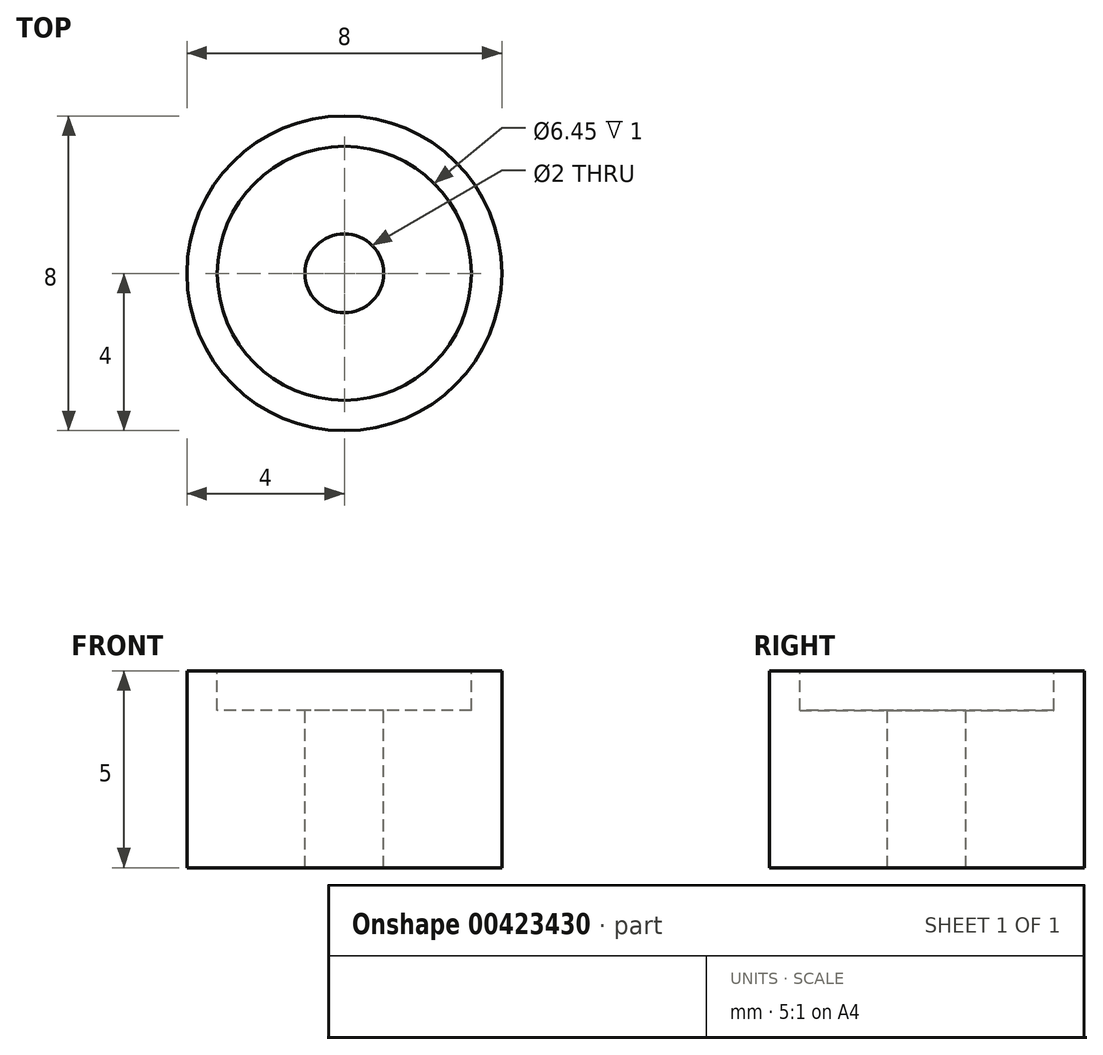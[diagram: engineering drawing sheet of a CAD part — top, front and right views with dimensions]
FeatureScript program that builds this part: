
annotation { "Feature Type Name" : "Feature", "Feature Type Description" : "" }
export const myFeature = defineFeature(function(context is Context, id is Id, definition is map)
    precondition{}
    {
        {
            var Q0;
            Q0=qCreatedBy(makeId("Top.planeOp"),FACE);
            var sketch = newSketch(context, id + "F0", { "sketchPlane" : qUnion([Q0])});
            skCircle(sketch, "E0", {"center": v(0, 0) * mm, "radius": 4 * mm});
            skSolve(sketch);
        }
        {
            var Q0;
            Q0 = qSketchRegion(id + "F0", true);
            extrude(context, id + "F1", {"entities" : qUnion([Q0]), "depth" : 5 * mm});
        }
        {
            var Q0;
            Q0=makeQuery(id+"F1.opExtrude","CAP_FACE",FACE,{"disambiguationData":[OSD([sQuery(id+"F0.wireOp",EDGE,"E0")])],"isStart":false});
            var sketch = newSketch(context, id + "F2", { "sketchPlane" : qUnion([Q0])});
            skCircle(sketch, "E1", {"center": v(0, 0) * mm, "radius": 3.23 * mm});
            skSolve(sketch);
        }
        {
            var Q0;
            Q0 = qSketchRegion(id + "F2", true);
            extrude(context, id + "F3", {"entities" : qUnion([Q0]), "operationType" : NewBodyOperationType.REMOVE, "oppositeDirection" : true, "depth" : 1 * mm});
        }
        {
            var Q0;
            Q0=makeQuery(id+"F3.boolean.opBoolean","COPY",FACE,{"derivedFrom":makeQuery(id+"F3.opExtrude","CAP_FACE",FACE,{"disambiguationData":[OSD([sQuery(id+"F2.wireOp",EDGE,"E1")])],"isStart":false})});
            var sketch = newSketch(context, id + "F4", { "sketchPlane" : qUnion([Q0])});
            skCircle(sketch, "E2", {"center": v(0, 0) * mm, "radius": 1 * mm});
            skSolve(sketch);
        }
        {
            var Q0;
            Q0=makeQuery(id+"F4.imprint","IMPRINT",FACE,{"disambiguationData":[TD([[makeQuery(id+"F4.imprint","IMPRINT",EDGE,{"derivedFrom":sQuery(id+"F4.wireOp",EDGE,"E2")}),1.0]])]});
            extrude(context, id + "F5", {"entities" : qUnion([Q0]), "operationType" : NewBodyOperationType.REMOVE, "endBound" : BoundingType.THROUGH_ALL, "oppositeDirection" : true, "depth" : 25 * mm});
        }
    });
